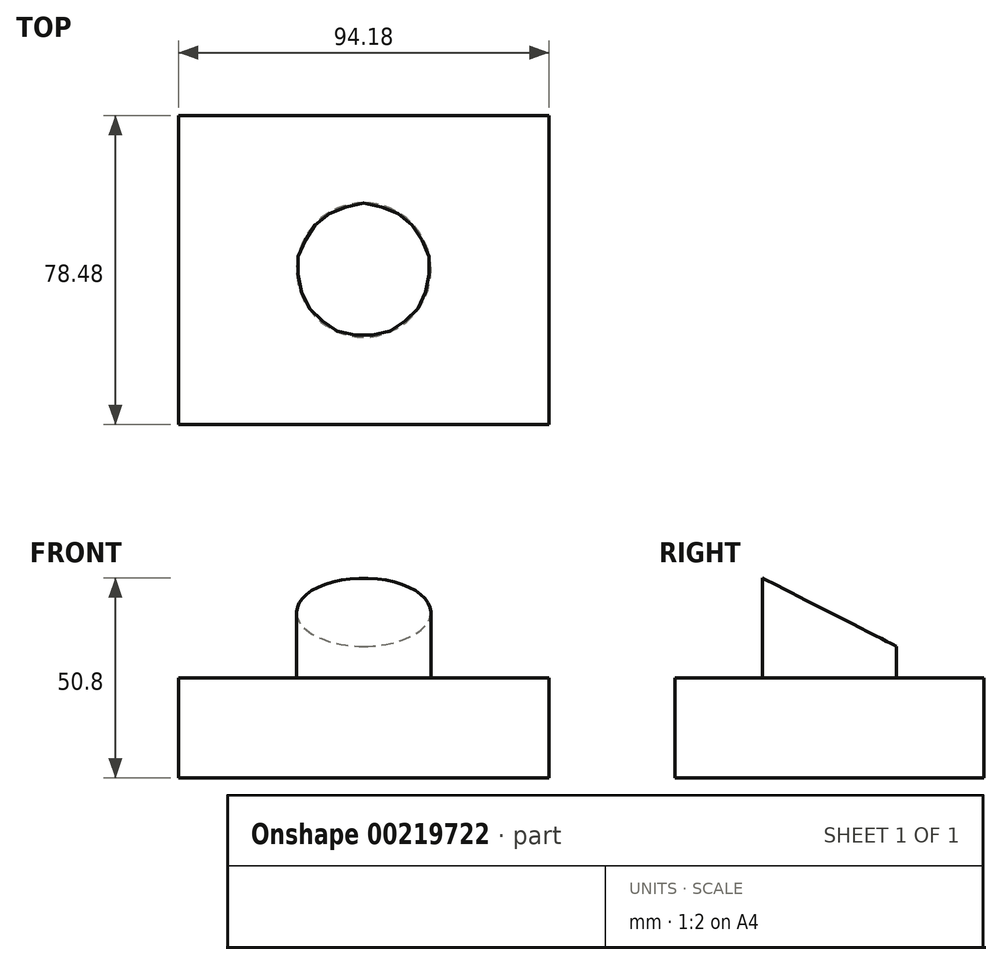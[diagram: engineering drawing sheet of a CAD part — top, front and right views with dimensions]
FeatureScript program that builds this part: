
annotation { "Feature Type Name" : "Feature", "Feature Type Description" : "" }
export const myFeature = defineFeature(function(context is Context, id is Id, definition is map)
    precondition{}
    {
        {
            var Q0;
            Q0=qCreatedBy(makeId("Top.planeOp"),FACE);
            var sketch = newSketch(context, id + "F0", { "sketchPlane" : qUnion([Q0])});
            skLineSegment(sketch, "E0.bottom", {"start": v(47.09, 39.24) * mm, "end": v(-47.09, 39.24) * mm});
            skLineSegment(sketch, "E0.top", {"start": v(47.09, -39.24) * mm, "end": v(-47.09, -39.24) * mm});
            skLineSegment(sketch, "E0.left", {"start": v(47.09, 39.24) * mm, "end": v(47.09, -39.24) * mm});
            skLineSegment(sketch, "E0.right", {"start": v(-47.09, 39.24) * mm, "end": v(-47.09, -39.24) * mm});
            skPoint(sketch, "E0.middle", {"position": v(0, 0) * mm});
            skSolve(sketch);
        }
        {
            var Q0;
            Q0=makeQuery(id+"F0.imprint","IMPRINT",FACE,{"disambiguationData":[TD([[makeQuery(id+"F0.imprint","IMPRINT",EDGE,{"derivedFrom":sQuery(id+"F0.wireOp",EDGE,"E0.bottom")}),1.0]])]});
            extrude(context, id + "F1", {"entities" : qUnion([Q0]), "depth" : 25.4 * mm});
        }
        {
            var Q0;
            Q0=makeQuery(id+"F1.opExtrude","CAP_FACE",FACE,{"disambiguationData":[OSD([sQuery(id+"F0.wireOp",EDGE,"E0.bottom"),sQuery(id+"F0.wireOp",EDGE,"E0.top"),sQuery(id+"F0.wireOp",EDGE,"E0.left"),sQuery(id+"F0.wireOp",EDGE,"E0.right")])],"isStart":false});
            var sketch = newSketch(context, id + "F2", { "sketchPlane" : qUnion([Q0])});
            skCircle(sketch, "E1", {"center": v(0, 0) * mm, "radius": 17.06 * mm});
            skSolve(sketch);
        }
        {
            var Q0;
            Q0=makeQuery(id+"F2.imprint","IMPRINT",FACE,{"disambiguationData":[TD([[makeQuery(id+"F2.imprint","IMPRINT",EDGE,{"derivedFrom":sQuery(id+"F2.wireOp",EDGE,"E1")}),1.0]])]});
            extrude(context, id + "F3", {"entities" : qUnion([Q0]), "operationType" : NewBodyOperationType.ADD, "depth" : 25.4 * mm});
        }
        {
            var Q0;
            Q0=makeQuery(id+"F1.opExtrude","SWEPT_FACE",FACE,{"disambiguationData":[OSD([sQuery(id+"F0.wireOp",EDGE,"E0.left")])]});
            var sketch = newSketch(context, id + "F4", { "sketchPlane" : qUnion([Q0])});
            skLineSegment(sketch, "E2.0", {"start": v(-17.06, 50.8) * mm, "end": v(17.06, 50.8) * mm});
            skLineSegment(sketch, "E3", {"start": v(17.06, 50.8) * mm, "end": v(17.06, 25.4) * mm});
            skLineSegment(sketch, "E4", {"start": v(-17.06, 50.8) * mm, "end": v(17.06, 33.43) * mm});
            skSolve(sketch);
        }
        {
            var Q0;
            {var subQ0=sQuery(id+"F4.wireOp",EDGE,"E2.0");Q0=makeQuery(id+"F4.imprint","IMPRINT",FACE,{"disambiguationData":[TD([[makeQuery(id+"F4.imprint","IMPRINT",EDGE,{"derivedFrom":subQ0}),-1.0]])]});}
            extrude(context, id + "F5", {"entities" : qUnion([Q0]), "operationType" : NewBodyOperationType.REMOVE, "endBound" : BoundingType.THROUGH_ALL, "oppositeDirection" : true, "depth" : 25.4 * mm});
        }
    });
